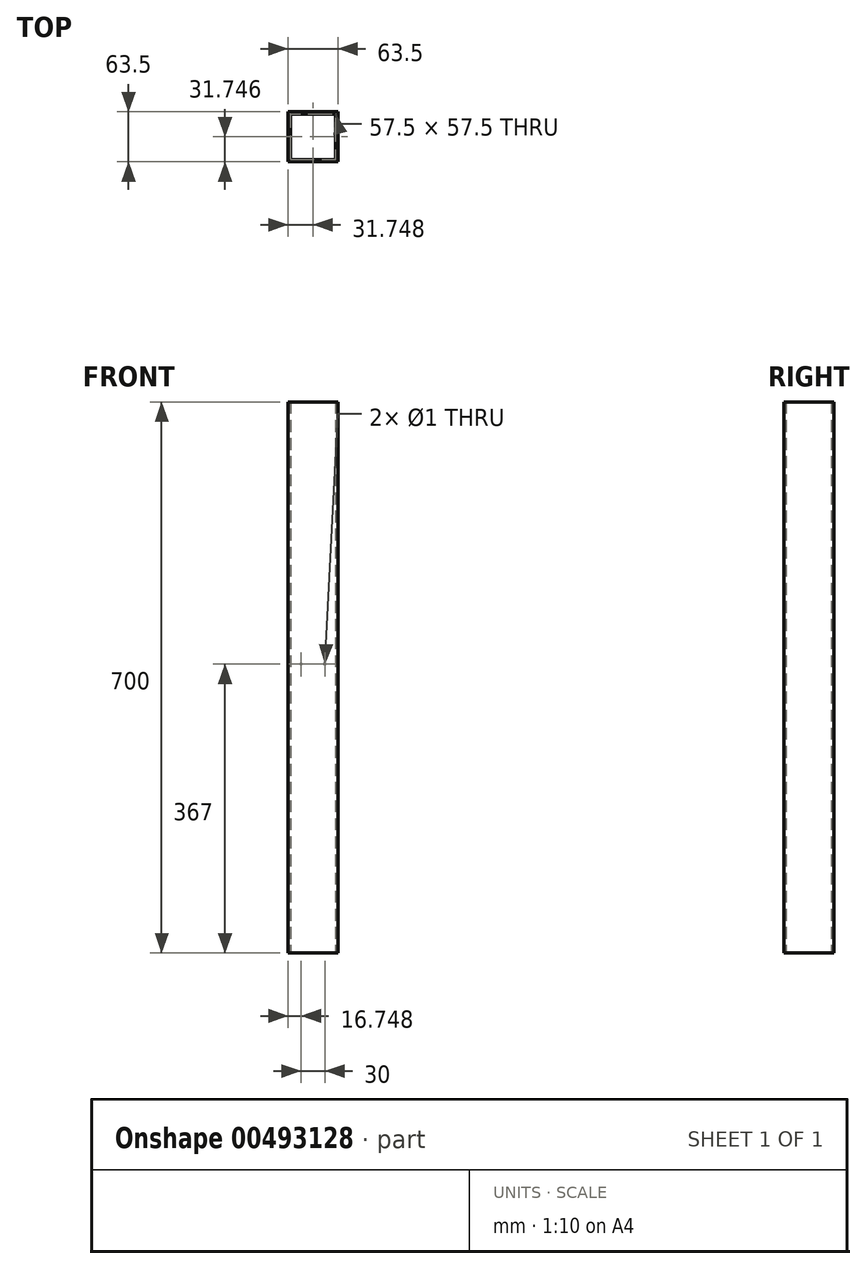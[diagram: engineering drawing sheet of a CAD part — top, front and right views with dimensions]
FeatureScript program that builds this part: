
annotation { "Feature Type Name" : "Feature", "Feature Type Description" : "" }
export const myFeature = defineFeature(function(context is Context, id is Id, definition is map)
    precondition{}
    {
        {
            var Q0;
            Q0=qCreatedBy(makeId("Top.planeOp"),FACE);
            var sketch = newSketch(context, id + "F0", { "sketchPlane" : qUnion([Q0])});
            skLineSegment(sketch, "E0.bottom", {"start": v(-32.2, 11.96) * mm, "end": v(25.3, 11.96) * mm});
            skLineSegment(sketch, "E0.top", {"start": v(-32.2, -45.54) * mm, "end": v(25.3, -45.54) * mm});
            skLineSegment(sketch, "E0.left", {"start": v(-32.2, 11.96) * mm, "end": v(-32.2, -45.54) * mm});
            skLineSegment(sketch, "E0.right", {"start": v(25.3, 11.96) * mm, "end": v(25.3, -45.54) * mm});
            skLineSegment(sketch, "E1.bottom", {"start": v(-35.2, 14.96) * mm, "end": v(28.3, 14.96) * mm});
            skLineSegment(sketch, "E1.top", {"start": v(-35.2, -48.54) * mm, "end": v(28.3, -48.54) * mm});
            skLineSegment(sketch, "E1.left", {"start": v(-35.2, 14.96) * mm, "end": v(-35.2, -48.54) * mm});
            skLineSegment(sketch, "E1.right", {"start": v(28.3, 14.96) * mm, "end": v(28.3, -48.54) * mm});
            skSolve(sketch);
        }
        {
            var Q0;
            Q0 = qSketchRegion(id + "F0", true);
            extrude(context, id + "F1", {"entities" : qUnion([Q0]), "offsetDistance" : 25 * mm, "depth" : 700 * mm});
        }
        {
            var Q0;
            Q0=makeQuery(id+"F1.opExtrude","SWEPT_FACE",FACE,{"disambiguationData":[OSD([sQuery(id+"F0.wireOp",EDGE,"E1.top")])]});
            var sketch = newSketch(context, id + "F2", { "sketchPlane" : qUnion([Q0])});
            skCircle(sketch, "E2", {"center": v(-18.45, 367) * mm, "radius": 0.5 * mm});
            skCircle(sketch, "E3", {"center": v(11.55, 367) * mm, "radius": 0.5 * mm});
            skSolve(sketch);
        }
        {
            var Q0;
            Q0 = qSketchRegion(id + "F2", true);
            extrude(context, id + "F3", {"entities" : qUnion([Q0]), "operationType" : NewBodyOperationType.REMOVE, "oppositeDirection" : true, "depth" : 3 * mm, "offsetDistance" : 25 * mm});
        }
    });
